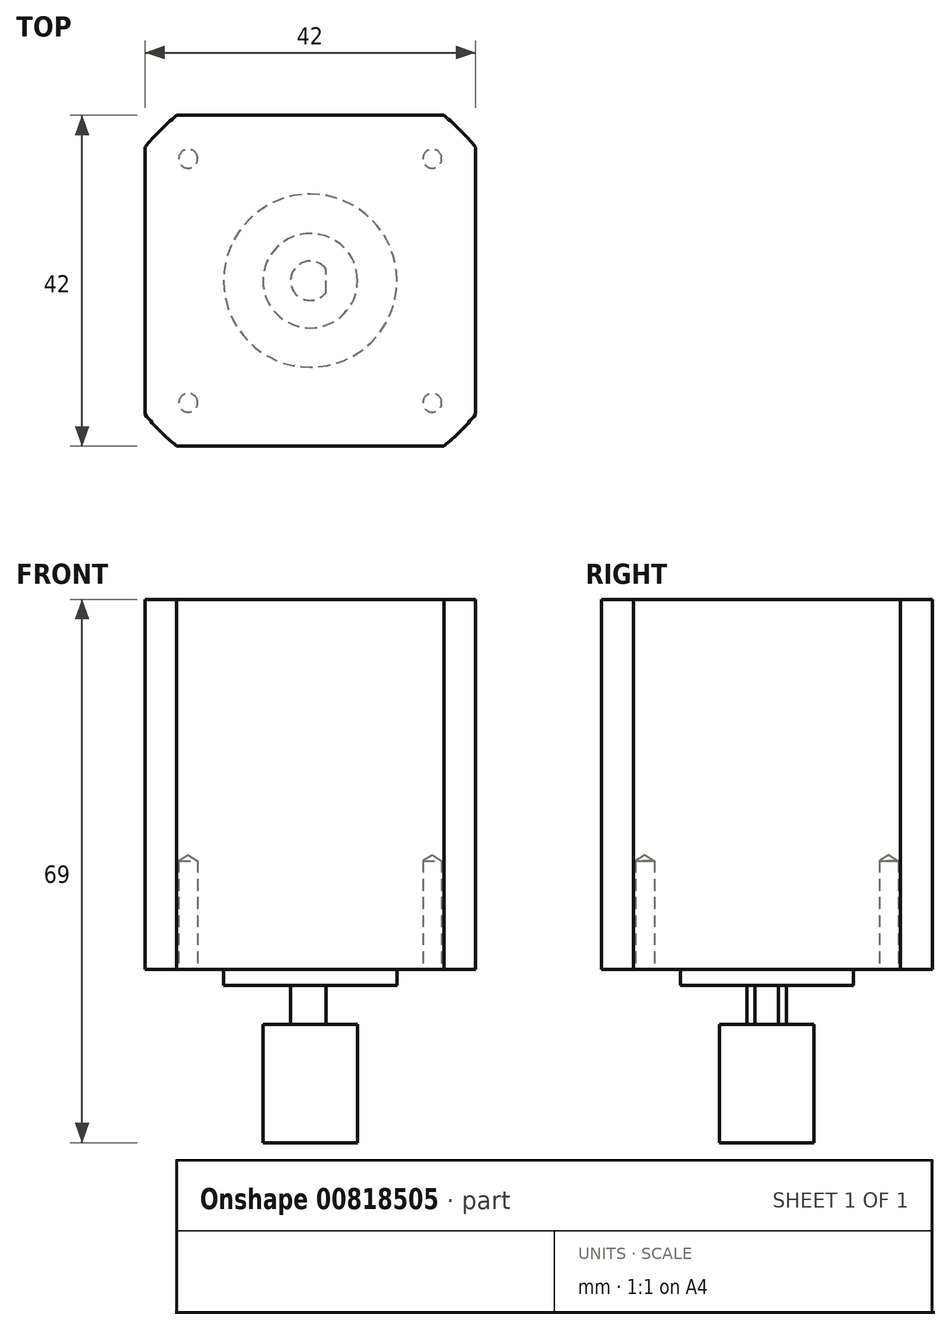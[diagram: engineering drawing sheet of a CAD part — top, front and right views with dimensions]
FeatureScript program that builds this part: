
annotation { "Feature Type Name" : "Feature", "Feature Type Description" : "" }
export const myFeature = defineFeature(function(context is Context, id is Id, definition is map)
    precondition{}
    {
        {
            var Q0;
            Q0=qCreatedBy(makeId("Top.planeOp"),FACE);
            var sketch = newSketch(context, id + "F0", { "sketchPlane" : qUnion([Q0])});
            skLineSegment(sketch, "E0.bottom", {"start": v(21, 21) * mm, "end": v(-21, 21) * mm});
            skLineSegment(sketch, "E0.top", {"start": v(21, -21) * mm, "end": v(-21, -21) * mm});
            skLineSegment(sketch, "E0.left", {"start": v(21, 21) * mm, "end": v(21, -21) * mm});
            skLineSegment(sketch, "E0.right", {"start": v(-21, 21) * mm, "end": v(-21, -21) * mm});
            skPoint(sketch, "E0.middle", {"position": v(0, 0) * mm});
            skCircle(sketch, "E1", {"center": v(0, 0) * mm, "radius": 27 * mm});
            skSolve(sketch);
        }
        {
            var Q0;
            {var subQ0=sQuery(id+"F0.wireOp",EDGE,"E1");var subQ7=sQuery(id+"F0.wireOp",EDGE,"E0.bottom");var subQ12=makeQuery(id+"F0.imprint","INTERSECT",VERTEX,{"disambiguationData":[OD(0.0)],"derivedFrom":[subQ7,subQ0]});Q0=makeQuery(id+"F0.imprint","IMPRINT",FACE,{"disambiguationData":[TD([[makeQuery(id+"F0.imprint","IMPRINT",EDGE,{"disambiguationData":[TD([[subQ12,-1.0]])],"derivedFrom":subQ7}),1.0]])]});}
            extrude(context, id + "F1", {"entities" : qUnion([Q0]), "depth" : 47 * mm});
        }
        {
            var Q0;
            Q0=makeQuery(id+"F1.opExtrude","CAP_FACE",FACE,{"disambiguationData":[OSD([sQuery(id+"F0.wireOp",EDGE,"E0.bottom"),sQuery(id+"F0.wireOp",EDGE,"E0.top"),sQuery(id+"F0.wireOp",EDGE,"E0.left"),sQuery(id+"F0.wireOp",EDGE,"E0.right"),sQuery(id+"F0.wireOp",EDGE,"E1")])],"isStart":true});
            var sketch = newSketch(context, id + "F2", { "sketchPlane" : qUnion([Q0])});
            skCircle(sketch, "E2", {"center": v(0, 0) * mm, "radius": 11 * mm});
            skLineSegment(sketch, "E3.bottom", {"start": v(15.5, 15.5) * mm, "end": v(-15.5, 15.5) * mm});
            skLineSegment(sketch, "E3.top", {"start": v(15.5, -15.5) * mm, "end": v(-15.5, -15.5) * mm});
            skLineSegment(sketch, "E3.left", {"start": v(15.5, 15.5) * mm, "end": v(15.5, -15.5) * mm});
            skLineSegment(sketch, "E3.right", {"start": v(-15.5, 15.5) * mm, "end": v(-15.5, -15.5) * mm});
            skSolve(sketch);
        }
        {
            var Q0;
            Q0=makeQuery(id+"F2.imprint","IMPRINT",FACE,{"disambiguationData":[TD([[makeQuery(id+"F2.imprint","IMPRINT",EDGE,{"derivedFrom":sQuery(id+"F2.wireOp",EDGE,"E2")}),1.0]])]});
            extrude(context, id + "F3", {"entities" : qUnion([Q0]), "operationType" : NewBodyOperationType.ADD, "depth" : 2 * mm});
        }
        {
            var Q0;
            Q0=sQuery(id+"F2.wireOp",VERTEX,"E3.right.start");
            var Q1;
            Q1=sQuery(id+"F2.wireOp",VERTEX,"E3.left.start");
            var Q2;
            Q2=sQuery(id+"F2.wireOp",VERTEX,"E3.left.end");
            var Q3;
            Q3=sQuery(id+"F2.wireOp",VERTEX,"E3.top.end");
            var Q4;
            Q4=makeQuery(id+"F1.opExtrude","SWEPT_BODY",BODY,{"disambiguationData":[OSD([sQuery(id+"F0.wireOp",EDGE,"E0.bottom"),sQuery(id+"F0.wireOp",EDGE,"E0.top"),sQuery(id+"F0.wireOp",EDGE,"E0.left"),sQuery(id+"F0.wireOp",EDGE,"E0.right"),sQuery(id+"F0.wireOp",EDGE,"E1")])]});
            hole(context, id + "F4", {"style" : HoleStyle.SIMPLE, "endStyle" : HoleEndStyle.BLIND, "standardTappedOrClearance" : lookupTablePath({ "standard" : "ISO", "engagement" : "75%", "pitch" : "0.6 mm", "size" : "M3", "type" : "Tapped" }), "standardBlindInLast" : lookupTablePath({ "standard" : "ISO", "engagement" : "75%", "pitch" : "0.6 mm", "size" : "M3", "type" : "Tapped" }), "holeDiameter" : 2.4 * mm, "showTappedDepth" : true, "holeDepth" : 13.8 * mm, "tappedDepth" : 12 * mm, "tapClearance" : 3, "locations" : qUnion([Q0, Q1, Q2, Q3]), "scope" : qUnion([Q4])});
        }
        {
            var Q0;
            Q0=makeQuery(id+"F3.opExtrude","CAP_FACE",FACE,{"disambiguationData":[OSD([sQuery(id+"F2.wireOp",EDGE,"E2")])],"isStart":false});
            var sketch = newSketch(context, id + "F5", { "sketchPlane" : qUnion([Q0])});
            skCircle(sketch, "E4", {"center": v(0, 0) * mm, "radius": 2.5 * mm});
            skLineSegment(sketch, "E5", {"start": v(2, 1.5) * mm, "end": v(2, -1.5) * mm});
            skSolve(sketch);
        }
        {
            var Q0;
            {var subQ0=sQuery(id+"F5.wireOp",EDGE,"E5");Q0=makeQuery(id+"F5.imprint","IMPRINT",FACE,{"disambiguationData":[TD([[makeQuery(id+"F5.imprint","IMPRINT",EDGE,{"derivedFrom":subQ0}),-1.0]])]});}
            extrude(context, id + "F6", {"entities" : qUnion([Q0]), "operationType" : NewBodyOperationType.ADD, "depth" : 20 * mm});
        }
        {
            var Q0;
            Q0=makeQuery(id+"F6.opExtrude","CAP_FACE",FACE,{"disambiguationData":[OSD([sQuery(id+"F5.wireOp",EDGE,"E4"),sQuery(id+"F5.wireOp",EDGE,"E5")])],"isStart":false});
            var sketch = newSketch(context, id + "F7", { "sketchPlane" : qUnion([Q0])});
            skCircle(sketch, "E6", {"center": v(0, 0) * mm, "radius": 6 * mm});
            skSolve(sketch);
        }
        {
            var Q0;
            Q0=qSketchRegion(id+"F7",true);
            extrude(context, id + "F8", {"entities" : qUnion([Q0]), "operationType" : NewBodyOperationType.ADD, "oppositeDirection" : true, "depth" : 15 * mm});
        }
    });
